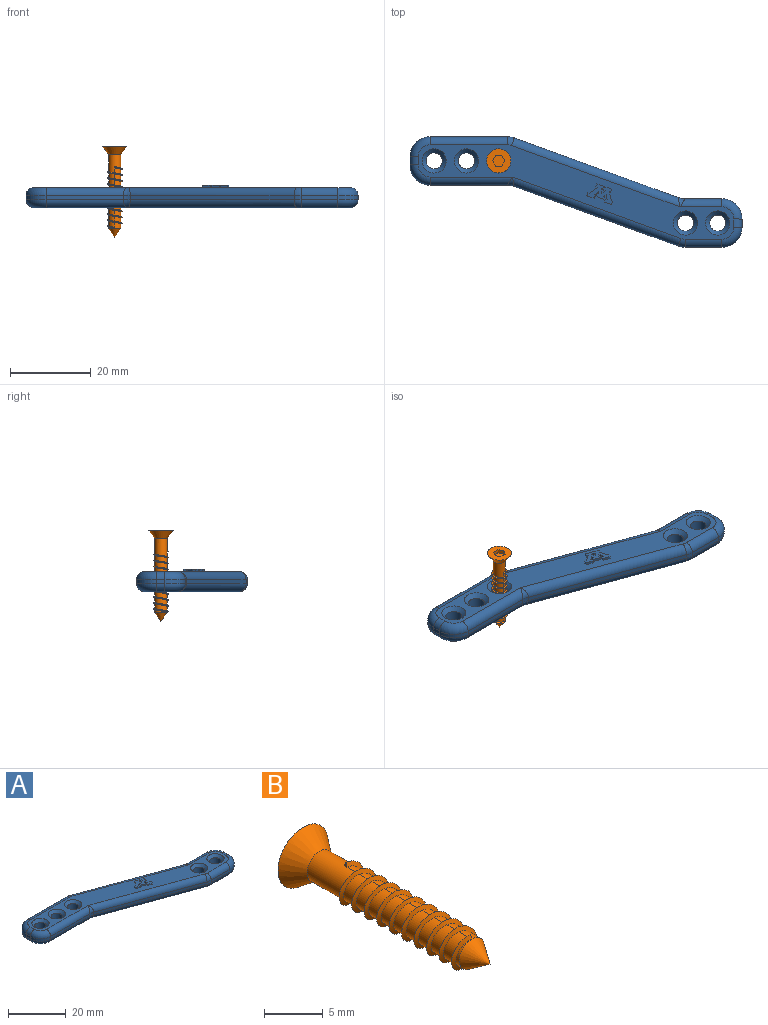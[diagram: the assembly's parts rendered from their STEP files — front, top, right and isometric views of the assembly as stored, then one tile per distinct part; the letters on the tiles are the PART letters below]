
ASSEMBLY  parts=2 mates=1
PART A: 94 faces, bbox 83.1x28.2x5.6 mm
  f0: plane 78.29x23.39mm, normal (0,0,1), area 452.6mm2, adj f23,f24,f25,f26,f27,f28,f29,f30
  f1: plane 78.29x23.39mm, normal (0,0,-1), area 544.8mm2, adj f10,f11,f12,f13,f14,f15,f16,f17
  f2: plane 2x1mm, normal (-1,0,0), area 2mm2, adj f18,f26,f44,f47
  f3: plane 19.12x1mm, normal (0,-1,0), area 19.1mm2, adj f16,f24,f47,f50
  f4: plane 40.63x14.79mm, normal (-0.34,-0.94,0), area 43.2mm2, adj f15,f23,f41,f50
  f5: plane 9.12x1mm, normal (0,-1,0), area 9.1mm2, adj f17,f25,f38,f41
  f6: plane 2x1mm, normal (1,0,0), area 2mm2, adj f19,f27,f35,f38
  f7: plane 9.12x1mm, normal (0,1,0), area 9.1mm2, adj f21,f29,f35,f53
  f8: plane 40.63x14.79mm, normal (0.34,0.94,0), area 43.2mm2, adj f22,f30,f32,f53
  f9: plane 19.12x1mm, normal (0,1,0), area 19.1mm2, adj f20,f28,f32,f44
  f10: cylinder r=2mm len=4mm, axis (0,0,1), area 50.3mm2, adj f1,f55
  f11: cylinder r=2mm len=4mm, axis (0,0,1), area 50.3mm2, adj f1,f58
  f12: cylinder r=2mm len=4mm, axis (0,0,1), area 50.3mm2, adj f1,f59
  f13: cylinder r=2mm len=4mm, axis (0,0,1), area 50.3mm2, adj f1,f56
  f14: cylinder r=2mm len=4mm, axis (0,0,1), area 50.3mm2, adj f1,f57
  f15: cylinder r=2mm len=42.47mm, axis (0.94,-0.34,0), area 137.2mm2, adj f1,f4,f42,f49
  f16: cylinder r=2mm len=20.35mm, axis (1,0,0), area 61.5mm2, adj f1,f3,f48,f49
  f17: cylinder r=2mm len=9.12mm, axis (1,0,0), area 28.6mm2, adj f1,f5,f39,f42
  f18: cylinder r=2mm len=2mm, axis (0,-1,0), area 6.3mm2, adj f1,f2,f45,f48
  f19: cylinder r=2mm len=2mm, axis (0,1,0), area 6.3mm2, adj f1,f6,f36,f39
  f20: cylinder r=2mm len=19.12mm, axis (-1,0,0), area 60.1mm2, adj f1,f9,f33,f45
  f21: cylinder r=2mm len=10.35mm, axis (-1,0,0), area 30.1mm2, adj f1,f7,f36,f52
  f22: cylinder r=2mm len=42.47mm, axis (-0.94,0.34,0), area 137.2mm2, adj f1,f8,f33,f52
  f23: cylinder r=2mm len=42.47mm, axis (-0.94,0.34,0), area 137.2mm2, adj f0,f4,f40,f51
  f24: cylinder r=2mm len=20.35mm, axis (-1,0,0), area 61.5mm2, adj f0,f3,f46,f51
  f25: cylinder r=2mm len=9.12mm, axis (-1,0,0), area 28.6mm2, adj f0,f5,f37,f40
  f26: cylinder r=2mm len=2mm, axis (0,1,0), area 6.3mm2, adj f0,f2,f43,f46
  f27: cylinder r=2mm len=2mm, axis (0,-1,0), area 6.3mm2, adj f0,f6,f34,f37
  f28: cylinder r=2mm len=19.12mm, axis (1,0,0), area 60.1mm2, adj f0,f9,f31,f43
  f29: cylinder r=2mm len=10.35mm, axis (1,0,0), area 30.1mm2, adj f0,f7,f34,f54
  f30: cylinder r=2mm len=42.47mm, axis (0.94,-0.34,0), area 137.2mm2, adj f0,f8,f31,f54
  f31: torus R=3mm, axis (0,0,1), area 4.7mm2, adj f0,f28,f30,f32
  f32: cylinder r=5mm len=1.71mm, axis (0,0,-1), area 1.7mm2, adj f8,f9,f31,f33
  f33: torus R=3mm, axis (0,0,1), area 4.7mm2, adj f1,f20,f22,f32
  f34: torus R=3mm, axis (0,0,1), area 21.1mm2, adj f0,f27,f29,f35
  f35: cylinder r=5mm len=5mm, axis (0,0,1), area 7.9mm2, adj f6,f7,f34,f36
  f36: torus R=3mm, axis (0,0,1), area 21.1mm2, adj f1,f19,f21,f35
  f37: torus R=3mm, axis (0,0,1), area 21.1mm2, adj f0,f25,f27,f38
  f38: cylinder r=5mm len=5mm, axis (0,0,-1), area 7.9mm2, adj f5,f6,f37,f39
  f39: torus R=3mm, axis (0,0,1), area 21.1mm2, adj f1,f17,f19,f38
  f40: torus R=3mm, axis (0,0,1), area 4.7mm2, adj f0,f23,f25,f41
  f41: cylinder r=5mm len=1.71mm, axis (0,0,-1), area 1.7mm2, adj f4,f5,f40,f42
  f42: torus R=3mm, axis (0,0,1), area 4.7mm2, adj f1,f15,f17,f41
  f43: torus R=3mm, axis (0,0,1), area 21.1mm2, adj f0,f26,f28,f44
  f44: cylinder r=5mm len=5mm, axis (0,0,1), area 7.9mm2, adj f2,f9,f43,f45
  f45: torus R=3mm, axis (0,0,1), area 21.1mm2, adj f1,f18,f20,f44
  f46: torus R=3mm, axis (0,0,1), area 21.1mm2, adj f0,f24,f26,f47
  f47: cylinder r=5mm len=5mm, axis (0,0,-1), area 7.9mm2, adj f2,f3,f46,f48
  f48: torus R=3mm, axis (0,0,1), area 21.1mm2, adj f1,f16,f18,f47
  f49: bspline ~2.3x2.26mm, area 3.5mm2, adj f15,f16,f50
  f50: cylinder r=5mm len=1.71mm, axis (0,0,1), area 1.7mm2, adj f3,f4,f49,f51
  f51: bspline ~2.3x2.26mm, area 3.5mm2, adj f23,f24,f50
  f52: bspline ~2.3x2.26mm, area 3.5mm2, adj f21,f22,f53
  f53: cylinder r=5mm len=1.71mm, axis (0,0,1), area 1.7mm2, adj f7,f8,f52,f54
  f54: bspline ~2.3x2.26mm, area 3.5mm2, adj f29,f30,f53
  f55: cone r=2mm half-angle=45deg, axis (0,0,1), area 22.2mm2, adj f0,f10
  f56: cone r=2mm half-angle=45deg, axis (0,0,1), area 22.2mm2, adj f0,f13
  f57: cone r=2mm half-angle=45deg, axis (0,0,1), area 22.2mm2, adj f0,f14
  f58: cone r=2mm half-angle=45deg, axis (0,0,1), area 22.2mm2, adj f0,f11
  f59: cone r=2mm half-angle=45deg, axis (0,0,1), area 22.2mm2, adj f0,f12
  f60: plane 2.01x1.45mm, normal (-0.59,0.81,0), area 1.5mm2, adj f0,f61,f92,f93
  f61: plane 0.6x0.38mm, normal (0.39,0.92,0), area 0.2mm2, adj f0,f60,f62,f93
  f62: plane 0.75x0.6mm, normal (-0.94,0.33,0), area 0.5mm2, adj f0,f61,f63,f93
  f63: plane 1.79x0.65mm, normal (-0.34,-0.94,0), area 1.1mm2, adj f0,f62,f64,f93
  f64: plane 0.75x0.6mm, normal (0.94,-0.34,0), area 0.5mm2, adj f0,f63,f65,f93
  f65: plane 0.6x0.27mm, normal (0.34,0.94,0), area 0.2mm2, adj f0,f64,f66,f93
  f66: plane 1.01x0.73mm, normal (0.59,-0.81,0), area 0.8mm2, adj f0,f65,f67,f93
  f67: plane 0.6x0.51mm, normal (-0.98,-0.2,0), area 0.3mm2, adj f0,f66,f68,f93
  f68: plane 0.6x0.36mm, normal (0.34,0.94,0), area 0.2mm2, adj f0,f67,f69,f93
  f69: plane 0.79x0.6mm, normal (-0.94,0.34,0), area 0.5mm2, adj f0,f68,f70,f93
  f70: plane 1.91x0.69mm, normal (-0.34,-0.94,0), area 1.2mm2, adj f0,f69,f71,f93
  f71: plane 0.69x0.6mm, normal (0.94,-0.34,0), area 0.4mm2, adj f0,f70,f72,f93
  f72: plane 0.6x0.27mm, normal (0.34,0.94,0), area 0.2mm2, adj f0,f71,f73,f93
  f73: plane 0.65x0.6mm, normal (0.6,-0.8,0), area 0.5mm2, adj f0,f72,f74,f93
  f74: plane 1.43x0.6mm, normal (-0.98,-0.17,0), area 0.9mm2, adj f0,f73,f75,f93
  f75: plane 0.6x0.46mm, normal (0.34,0.94,0), area 0.3mm2, adj f0,f74,f76,f93
  f76: plane 0.68x0.6mm, normal (-0.94,0.34,0), area 0.4mm2, adj f0,f75,f77,f93
  f77: plane 1.79x0.65mm, normal (-0.34,-0.94,0), area 1.1mm2, adj f0,f76,f78,f93
  f78: plane 0.84x0.6mm, normal (0.94,-0.34,0), area 0.5mm2, adj f0,f77,f79,f93
  f79: plane 0.6x0.31mm, normal (0.34,0.94,0), area 0.2mm2, adj f0,f78,f80,f93
  f80: plane 2.21x0.61mm, normal (0.96,0.27,0), area 1.4mm2, adj f0,f79,f81,f93
  f81: plane 0.6x0.3mm, normal (-0.51,-0.86,0), area 0.2mm2, adj f0,f80,f82,f93
  f82: plane 0.84x0.6mm, normal (0.94,-0.34,0), area 0.5mm2, adj f0,f81,f83,f93
  f83: plane 1.67x0.61mm, normal (0.34,0.94,0), area 1.1mm2, adj f0,f82,f84,f93
  f84: plane 0.85x0.6mm, normal (-0.94,0.34,0), area 0.5mm2, adj f0,f83,f85,f93
  f85: plane 0.6x0.41mm, normal (-0.34,-0.94,0), area 0.3mm2, adj f0,f84,f86,f93
  f86: plane 0.81x0.6mm, normal (-0.59,0.81,0), area 0.6mm2, adj f0,f85,f87,f93
  f87: plane 1.05x0.6mm, normal (0.98,0.2,0), area 0.6mm2, adj f0,f86,f88,f93
  f88: plane 0.6x0.33mm, normal (-0.34,-0.94,0), area 0.2mm2, adj f0,f87,f89,f93
  f89: plane 0.74x0.6mm, normal (0.94,-0.34,0), area 0.5mm2, adj f0,f88,f90,f93
  f90: plane 1.64x0.6mm, normal (0.34,0.94,0), area 1mm2, adj f0,f89,f91,f93
  f91: plane 0.69x0.6mm, normal (-0.94,0.34,0), area 0.4mm2, adj f0,f90,f92,f93
  f92: plane 0.6x0.42mm, normal (-0.34,-0.94,0), area 0.3mm2, adj f0,f60,f91,f93
  f93: plane 6.43x5.12mm, normal (0,0,1), area 13.7mm2, adj f60,f61,f62,f63,f64,f65,f66,f67
PART B: 25 faces, bbox 6x22.5x6 mm
  f0: plane 6x6mm, normal (0,1,0), area 22.4mm2, adj f12,f18,f19,f20,f21,f22,f23
  f1: cylinder r=1.5mm len=4.5mm, axis (0,1,0), area 35.3mm2, adj f2,f12,f13,f15
  f2: cylinder r=1.5mm len=3mm, axis (0,1,0), area 11.3mm2, adj f1,f3,f15,f16
  f3: cylinder r=1.5mm len=3mm, axis (0,1,0), area 11.3mm2, adj f2,f4,f15,f16
  f4: cylinder r=1.5mm len=3mm, axis (0,1,0), area 11.3mm2, adj f3,f5,f15,f16
  f5: cylinder r=1.5mm len=3mm, axis (0,1,0), area 11.3mm2, adj f4,f6,f15,f16
  f6: cylinder r=1.5mm len=3mm, axis (0,1,0), area 11.3mm2, adj f5,f7,f15,f16
  f7: cylinder r=1.5mm len=3mm, axis (0,1,0), area 11.3mm2, adj f6,f8,f15,f16
  f8: cylinder r=1.5mm len=3mm, axis (0,1,0), area 11.3mm2, adj f7,f9,f15,f16
  f9: cylinder r=1.5mm len=3mm, axis (0,1,0), area 11.3mm2, adj f8,f10,f15,f16
  f10: cylinder r=1.5mm len=3mm, axis (0,1,0), area 11.3mm2, adj f9,f11,f15,f16
  f11: cylinder r=1.5mm len=3mm, axis (0,1,0), area 7.1mm2, adj f10,f14,f16,f17
  f12: cone r=1.5mm half-angle=36.9deg, axis (0,1,0), area 35.3mm2, adj f0,f1
  f13: plane 0.4x0.3mm, normal (-1,0,0), area 0.1mm2, adj f1,f15,f16
  f14: plane 0.4x0.3mm, normal (1,0,0), area 0.1mm2, adj f11,f15,f16
  f15: bspline ~15.15x4.39mm, area 45.9mm2, adj f1,f2,f3,f4,f5,f6,f7,f8
  f16: bspline ~15.15x4.39mm, area 46mm2, adj f2,f3,f4,f5,f6,f7,f8,f9
  f17: cone r=1.5mm half-angle=34.3deg, axis (0,1,0), area 12.5mm2, adj f11
  f18: plane 1.5x1mm, normal (0,0,-1), area 1.5mm2, adj f0,f19,f23,f24
  f19: plane 1.3x1mm, normal (-0.87,0,-0.5), area 1.5mm2, adj f0,f18,f20,f24
  f20: plane 1.3x1mm, normal (-0.87,0,0.5), area 1.5mm2, adj f0,f19,f21,f24
  f21: plane 1.5x1mm, normal (0,0,1), area 1.5mm2, adj f0,f20,f22,f24
  f22: plane 1.3x1mm, normal (0.87,0,0.5), area 1.5mm2, adj f0,f21,f23,f24
  f23: plane 1.3x1mm, normal (0.87,0,-0.5), area 1.5mm2, adj f0,f18,f22,f24
  f24: plane 3x2.6mm, normal (0,1,0), area 5.8mm2, adj f18,f19,f20,f21,f22,f23
PLACE A t=(-38.3,14.88,-3.48)mm
PLACE B rot(axis=(1,0,0),90deg) t=(-16.3,8.88,11.67)mm
MATE cylindrical B.f1 <-> A.f12  axis (0,0,1) through (-16.3,8.88,0.52)mm
